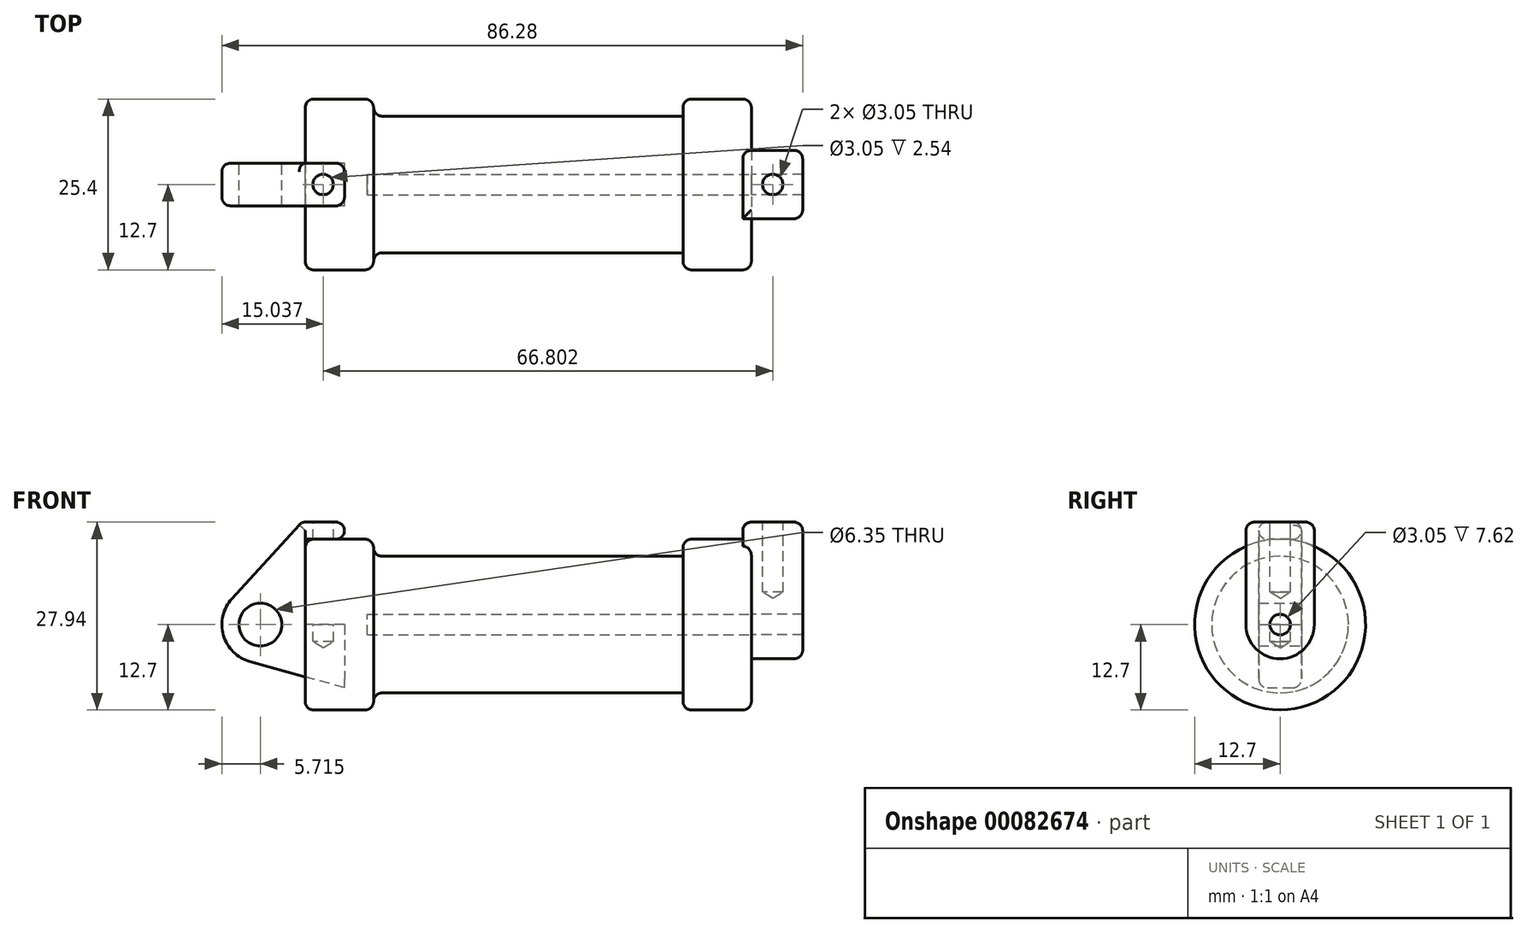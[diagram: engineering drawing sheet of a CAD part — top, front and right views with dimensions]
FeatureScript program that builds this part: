
annotation { "Feature Type Name" : "Feature", "Feature Type Description" : "" }
export const myFeature = defineFeature(function(context is Context, id is Id, definition is map)
    precondition{}
    {
        {
            var Q0;
            Q0=qCreatedBy(makeId("Front.planeOp"),FACE);
            var sketch = newSketch(context, id + "F0", { "sketchPlane" : qUnion([Q0])});
            skLineSegment(sketch, "E0", {"start": v(0, 0) * mm, "end": v(0, 12.7) * mm});
            skLineSegment(sketch, "E1", {"start": v(0, 12.7) * mm, "end": v(10.16, 12.7) * mm});
            skLineSegment(sketch, "E2", {"start": v(10.16, 12.7) * mm, "end": v(10.16, 10.16) * mm});
            skLineSegment(sketch, "E3", {"start": v(10.16, 10.16) * mm, "end": v(56.13, 10.16) * mm});
            skLineSegment(sketch, "E4", {"start": v(56.13, 10.16) * mm, "end": v(56.13, 12.7) * mm});
            skLineSegment(sketch, "E5", {"start": v(56.13, 12.7) * mm, "end": v(66.3, 12.7) * mm});
            skLineSegment(sketch, "E6", {"start": v(66.3, 12.7) * mm, "end": v(66.3, 0) * mm});
            skLineSegment(sketch, "E7", {"start": v(66.3, 0) * mm, "end": v(0, 0) * mm});
            skLineSegment(sketch, "E8", {"start": v(5.84, 15.24) * mm, "end": v(-0.5, 15.24) * mm});
            skLineSegment(sketch, "E9", {"start": v(-0.5, 15.24) * mm, "end": v(-10.88, 3.85) * mm});
            skLineSegment(sketch, "E10", {"start": v(0, 0) * mm, "end": v(-6.65, 0) * mm});
            skCircle(sketch, "E11", {"center": v(-6.65, 0) * mm, "radius": 5.72 * mm});
            skCircle(sketch, "E12", {"center": v(-6.65, 0) * mm, "radius": 3.18 * mm});
            skLineSegment(sketch, "E13", {"start": v(5.84, 15.24) * mm, "end": v(5.84, -9.4) * mm});
            skLineSegment(sketch, "E14", {"start": v(5.84, -9.4) * mm, "end": v(-8.18, -5.5) * mm});
            skSolve(sketch);
        }
        {
            var Q0;
            {var subQ0=sQuery(id+"F0.wireOp",EDGE,"E2");Q0=makeQuery(id+"F0.imprint","IMPRINT",FACE,{"disambiguationData":[TD([[makeQuery(id+"F0.imprint","IMPRINT",EDGE,{"derivedFrom":subQ0}),-1.0]])]});}
            var Q1;
            {var subQ0=sQuery(id+"F0.wireOp",EDGE,"E0");Q1=makeQuery(id+"F0.imprint","IMPRINT",FACE,{"disambiguationData":[TD([[makeQuery(id+"F0.imprint","IMPRINT",EDGE,{"derivedFrom":subQ0}),-1.0]])]});}
            var Q2;
            Q2=sQuery(id+"F0.wireOp",EDGE,"E7");
            revolve(context, id + "F1", {"entities" : qUnion([Q0, Q1]), "axis" : qUnion([Q2]), "revolveType" : RevolveType.FULL});
        }
        {
            var Q0;
            {var subQ3=sQuery(id+"F0.wireOp",EDGE,"E0");Q0=makeQuery(id+"F0.imprint","IMPRINT",FACE,{"disambiguationData":[TD([[makeQuery(id+"F0.imprint","IMPRINT",EDGE,{"derivedFrom":subQ3}),1.0]])]});}
            var Q1;
            {var subQ0=sQuery(id+"F0.wireOp",EDGE,"E14");Q1=makeQuery(id+"F0.imprint","IMPRINT",FACE,{"disambiguationData":[TD([[makeQuery(id+"F0.imprint","IMPRINT",EDGE,{"derivedFrom":subQ0}),-1.0]])]});}
            var Q2;
            {var subQ4=sQuery(id+"F0.wireOp",EDGE,"E12");Q2=makeQuery(id+"F0.imprint","IMPRINT",FACE,{"disambiguationData":[TD([[makeQuery(id+"F0.imprint","IMPRINT",EDGE,{"derivedFrom":subQ4}),-1.0]])]});}
            extrude(context, id + "F2", {"entities" : qUnion([Q0, Q1, Q2]), "endBound" : BoundingType.SYMMETRIC, "depth" : 6.35 * mm});
        }
        {
            var Q0;
            Q0=makeQuery(id+"F1.opRevolve","SWEPT_FACE",FACE,{"disambiguationData":[OSD([sQuery(id+"F0.wireOp",EDGE,"E6")])]});
            var sketch = newSketch(context, id + "F3", { "sketchPlane" : qUnion([Q0])});
            skCircle(sketch, "E15", {"center": v(0, 0) * mm, "radius": 5.08 * mm});
            skCircle(sketch, "E16", {"center": v(0, 0) * mm, "radius": 1.52 * mm});
            skLineSegment(sketch, "E17", {"start": v(-5.08, 0) * mm, "end": v(-5.08, 15.24) * mm});
            skLineSegment(sketch, "E18", {"start": v(5.08, 0) * mm, "end": v(5.08, 15.24) * mm});
            skLineSegment(sketch, "E19", {"start": v(-5.08, 15.24) * mm, "end": v(5.08, 15.24) * mm});
            skSolve(sketch);
        }
        {
            var Q0;
            Q0=makeQuery(id+"F3.imprint","IMPRINT",FACE,{"disambiguationData":[TD([[makeQuery(id+"F3.imprint","IMPRINT",EDGE,{"derivedFrom":sQuery(id+"F3.wireOp",EDGE,"E16")}),-1.0]])]});
            var Q1;
            {var subQ0=sQuery(id+"F3.wireOp",EDGE,"E17");var subQ1=sQuery(id+"F3.wireOp",EDGE,"E15");var subQ2=makeQuery(id+"F3.imprint","INTERSECT",VERTEX,{"derivedFrom":[subQ1,subQ0]});Q1=makeQuery(id+"F3.imprint","IMPRINT",FACE,{"disambiguationData":[TD([[makeQuery(id+"F3.imprint","IMPRINT",EDGE,{"disambiguationData":[TD([[subQ2,1.0]])],"derivedFrom":subQ1}),-1.0]])]});}
            var Q2;
            {var subQ0=sQuery(id+"F3.wireOp",EDGE,"E19");Q2=makeQuery(id+"F3.imprint","IMPRINT",FACE,{"disambiguationData":[TD([[makeQuery(id+"F3.imprint","IMPRINT",EDGE,{"derivedFrom":subQ0}),-1.0]])]});}
            extrude(context, id + "F4", {"entities" : qUnion([Q0, Q1, Q2]), "operationType" : NewBodyOperationType.ADD, "depth" : 7.62 * mm, "hasSecondDirection" : true, "secondDirectionOppositeDirection" : true, "secondDirectionDepth" : 1.27 * mm});
        }
        {
            var Q0;
            Q0=makeQuery(id+"F4.boolean.opBoolean","SPLIT",FACE,{"disambiguationData":[TD([makeQuery(id+"F4.opExtrude","SWEPT_FACE",FACE,{"disambiguationData":[OSD([sQuery(id+"F3.wireOp",EDGE,"E16")])]})])],"derivedFrom":makeQuery(id+"F1.opRevolve","SWEPT_FACE",FACE,{"disambiguationData":[OSD([sQuery(id+"F0.wireOp",EDGE,"E6")])]})});
            var sketch = newSketch(context, id + "F5", { "sketchPlane" : qUnion([Q0])});
            skCircle(sketch, "E20", {"center": v(0, 0) * mm, "radius": 1.52 * mm});
            skSolve(sketch);
        }
        {
            var Q0;
            Q0=makeQuery(id+"F5.imprint","IMPRINT",FACE,{"disambiguationData":[TD([[makeQuery(id+"F5.imprint","IMPRINT",EDGE,{"derivedFrom":sQuery(id+"F5.wireOp",EDGE,"E20")}),1.0]])]});
            extrude(context, id + "F6", {"entities" : qUnion([Q0]), "oppositeDirection" : true, "depth" : 57.04 * mm});
        }
        {
            var Q0;
            Q0=makeQuery(id+"F2.opExtrude","SWEPT_FACE",FACE,{"disambiguationData":[OSD([sQuery(id+"F0.wireOp",EDGE,"E8")])]});
            var sketch = newSketch(context, id + "F7", { "sketchPlane" : qUnion([Q0])});
            skLineSegment(sketch, "E21", {"start": v(-0.5, 3.18) * mm, "end": v(5.84, -3.18) * mm, "construction": true});
            skLineSegment(sketch, "E22", {"start": v(5.84, 3.18) * mm, "end": v(-0.5, -3.18) * mm, "construction": true});
            skCircle(sketch, "E23", {"center": v(2.67, 0) * mm, "radius": 1.53 * mm});
            skSolve(sketch);
        }
        {
            var Q0;
            Q0=sQuery(id+"F7.wireOp",VERTEX,"E23.center");
            var Q1;
            Q1=makeQuery(id+"F2.opExtrude","SWEPT_BODY",BODY,{"disambiguationData":[OSD([sQuery(id+"F0.wireOp",EDGE,"E0"),sQuery(id+"F0.wireOp",EDGE,"E1"),sQuery(id+"F0.wireOp",EDGE,"E7"),sQuery(id+"F0.wireOp",EDGE,"E8"),sQuery(id+"F0.wireOp",EDGE,"E9"),sQuery(id+"F0.wireOp",EDGE,"E11"),sQuery(id+"F0.wireOp",EDGE,"E12"),sQuery(id+"F0.wireOp",EDGE,"E13"),sQuery(id+"F0.wireOp",EDGE,"E14")])]});
            hole(context, id + "F8", {"style" : HoleStyle.SIMPLE, "endStyle" : HoleEndStyle.BLIND, "holeDiameter" : 3.05 * mm, "holeDepth" : 17.78 * mm, "locations" : qUnion([Q0]), "scope" : qUnion([Q1])});
        }
        {
            var Q0;
            Q0=makeQuery(id+"F4.opExtrude","SWEPT_FACE",FACE,{"disambiguationData":[OSD([sQuery(id+"F3.wireOp",EDGE,"E19")])]});
            var sketch = newSketch(context, id + "F9", { "sketchPlane" : qUnion([Q0])});
            skLineSegment(sketch, "E24", {"start": v(65.02, 5.08) * mm, "end": v(73.91, -5.08) * mm, "construction": true});
            skLineSegment(sketch, "E25", {"start": v(73.91, -5.08) * mm, "end": v(65.02, -5.08) * mm, "construction": true});
            skLineSegment(sketch, "E26", {"start": v(65.02, -5.08) * mm, "end": v(73.91, 5.08) * mm, "construction": true});
            skCircle(sketch, "E27", {"center": v(69.47, 0) * mm, "radius": 1.53 * mm});
            skSolve(sketch);
        }
        {
            var Q0;
            Q0=sQuery(id+"F9.wireOp",VERTEX,"E27.center");
            var Q1;
            Q1=makeQuery(id+"F1.opRevolve","SWEPT_BODY",BODY,{"disambiguationData":[OSD([sQuery(id+"F0.wireOp",EDGE,"E0"),sQuery(id+"F0.wireOp",EDGE,"E1"),sQuery(id+"F0.wireOp",EDGE,"E2"),sQuery(id+"F0.wireOp",EDGE,"E3"),sQuery(id+"F0.wireOp",EDGE,"E4"),sQuery(id+"F0.wireOp",EDGE,"E5"),sQuery(id+"F0.wireOp",EDGE,"E6"),sQuery(id+"F0.wireOp",EDGE,"E7")])]});
            hole(context, id + "F10", {"style" : HoleStyle.SIMPLE, "endStyle" : HoleEndStyle.BLIND, "holeDiameter" : 3.05 * mm, "holeDepth" : 10.4 * mm, "locations" : qUnion([Q0]), "scope" : qUnion([Q1])});
        }
        {
            var Q0;
            Q0=makeQuery(id+"F1.opRevolve","SWEPT_EDGE",EDGE,{"disambiguationData":[OSD([sQuery(id+"F0.wireOp",EDGE,"E1"),sQuery(id+"F0.wireOp",EDGE,"E2")])]});
            var Q1;
            Q1=makeQuery(id+"F1.opRevolve","SWEPT_EDGE",EDGE,{"disambiguationData":[OSD([sQuery(id+"F0.wireOp",EDGE,"E2"),sQuery(id+"F0.wireOp",EDGE,"E3")])]});
            var Q2;
            Q2=makeQuery(id+"F1.opRevolve","SWEPT_EDGE",EDGE,{"disambiguationData":[OSD([sQuery(id+"F0.wireOp",EDGE,"E4"),sQuery(id+"F0.wireOp",EDGE,"E5")])]});
            var Q3;
            Q3=makeQuery(id+"F1.opRevolve","SWEPT_EDGE",EDGE,{"disambiguationData":[OSD([sQuery(id+"F0.wireOp",EDGE,"E5"),sQuery(id+"F0.wireOp",EDGE,"E6")])]});
            var Q4;
            Q4=makeQuery(id+"F1.opRevolve","SWEPT_EDGE",EDGE,{"disambiguationData":[OSD([sQuery(id+"F0.wireOp",EDGE,"E0"),sQuery(id+"F0.wireOp",EDGE,"E1")])]});
            fillet(context, id + "F11", {"entities" : qUnion([Q0, Q1, Q2, Q3, Q4]), "radius" : 1.27 * mm, "tangentPropagation" : true, "allowEdgeOverflow" : false});
        }
        {
            var Q0;
            Q0=makeQuery(id+"F4.opExtrude","SWEPT_EDGE",EDGE,{"disambiguationData":[OSD([sQuery(id+"F3.wireOp",EDGE,"E17"),sQuery(id+"F3.wireOp",EDGE,"E19")])]});
            var Q1;
            Q1=makeQuery(id+"F4.opExtrude","CAP_EDGE",EDGE,{"disambiguationData":[OSD([sQuery(id+"F3.wireOp",EDGE,"E19")])],"isStart":false});
            var Q2;
            Q2=makeQuery(id+"F4.opExtrude","CAP_EDGE",EDGE,{"disambiguationData":[OSD([sQuery(id+"F3.wireOp",EDGE,"E17")])],"isStart":false});
            var Q3;
            Q3=makeQuery(id+"F4.opExtrude","CAP_EDGE",EDGE,{"disambiguationData":[OSD([sQuery(id+"F3.wireOp",EDGE,"E15")])],"isStart":false});
            var Q4;
            Q4=makeQuery(id+"F4.opExtrude","CAP_EDGE",EDGE,{"disambiguationData":[OSD([sQuery(id+"F3.wireOp",EDGE,"E18")])],"isStart":false});
            var Q5;
            Q5=makeQuery(id+"F4.opExtrude","CAP_EDGE",EDGE,{"disambiguationData":[OSD([sQuery(id+"F3.wireOp",EDGE,"E18")])],"isStart":true});
            var Q6;
            Q6=makeQuery(id+"F4.opExtrude","CAP_EDGE",EDGE,{"disambiguationData":[OSD([sQuery(id+"F3.wireOp",EDGE,"E19")])],"isStart":true});
            var Q7;
            Q7=makeQuery(id+"F4.opExtrude","SWEPT_EDGE",EDGE,{"disambiguationData":[OSD([sQuery(id+"F3.wireOp",EDGE,"E18"),sQuery(id+"F3.wireOp",EDGE,"E19")])]});
            fillet(context, id + "F12", {"entities" : qUnion([Q0, Q1, Q2, Q3, Q4, Q5, Q6, Q7]), "radius" : 1.27 * mm, "tangentPropagation" : true, "allowEdgeOverflow" : false});
        }
        {
            var Q0;
            Q0=makeQuery(id+"F2.opExtrude","SWEPT_EDGE",EDGE,{"disambiguationData":[OSD([sQuery(id+"F0.wireOp",EDGE,"E8"),sQuery(id+"F0.wireOp",EDGE,"E9")])]});
            var Q1;
            Q1=makeQuery(id+"F2.opExtrude","CAP_EDGE",EDGE,{"disambiguationData":[OSD([sQuery(id+"F0.wireOp",EDGE,"E8")])],"isStart":false});
            var Q2;
            Q2=makeQuery(id+"F2.opExtrude","CAP_EDGE",EDGE,{"disambiguationData":[OSD([sQuery(id+"F0.wireOp",EDGE,"E9")])],"isStart":false});
            var Q3;
            Q3=makeQuery(id+"F2.opExtrude","CAP_EDGE",EDGE,{"disambiguationData":[OSD([sQuery(id+"F0.wireOp",EDGE,"E11")])],"isStart":false});
            var Q4;
            Q4=makeQuery(id+"F2.opExtrude","CAP_EDGE",EDGE,{"disambiguationData":[OSD([sQuery(id+"F0.wireOp",EDGE,"E14")])],"isStart":false});
            var Q5;
            Q5=makeQuery(id+"F2.opExtrude","CAP_EDGE",EDGE,{"disambiguationData":[OSD([sQuery(id+"F0.wireOp",EDGE,"E11")])],"isStart":true});
            var Q6;
            Q6=makeQuery(id+"F2.opExtrude","CAP_EDGE",EDGE,{"disambiguationData":[OSD([sQuery(id+"F0.wireOp",EDGE,"E9")])],"isStart":true});
            var Q7;
            Q7=makeQuery(id+"F2.opExtrude","CAP_EDGE",EDGE,{"disambiguationData":[OSD([sQuery(id+"F0.wireOp",EDGE,"E14")])],"isStart":true});
            var Q8;
            {var subQ0=sQuery(id+"F0.wireOp",EDGE,"E13");Q8=makeQuery(id+"F2.opExtrude","CAP_EDGE",EDGE,{"disambiguationData":[OSD([subQ0]),TDD([makeQuery(id+"F0.imprint","IMPRINT",EDGE,{"disambiguationData":[TD([[makeQuery(id+"F0.imprint","INTERSECT",VERTEX,{"derivedFrom":[sQuery(id+"F0.wireOp",EDGE,"E8"),subQ0]}),-1.0]])],"derivedFrom":subQ0})])],"isStart":true});}
            var Q9;
            Q9=makeQuery(id+"F2.opExtrude","SWEPT_EDGE",EDGE,{"disambiguationData":[OSD([sQuery(id+"F0.wireOp",EDGE,"E8"),sQuery(id+"F0.wireOp",EDGE,"E13")])]});
            fillet(context, id + "F13", {"entities" : qUnion([Q0, Q1, Q2, Q3, Q4, Q5, Q6, Q7, Q8, Q9]), "radius" : 1.27 * mm, "tangentPropagation" : true, "allowEdgeOverflow" : false});
        }
        {
            var Q0;
            Q0=makeQuery(id+"F2.opExtrude","CAP_EDGE",EDGE,{"disambiguationData":[OSD([sQuery(id+"F0.wireOp",EDGE,"E8")])],"isStart":true});
            var Q1;
            {var subQ0=sQuery(id+"F0.wireOp",EDGE,"E8");Q1=makeQuery(id+"F13.opFillet","BLEND_EDGE",EDGE,{"blendedFrom":[makeQuery(id+"F2.opExtrude","SWEPT_EDGE",EDGE,{"disambiguationData":[OSD([subQ0,sQuery(id+"F0.wireOp",EDGE,"E13")])]}),makeQuery(id+"F2.opExtrude","CAP_EDGE",EDGE,{"disambiguationData":[OSD([subQ0])],"isStart":false})],"blendedInto":[]});}
            fillet(context, id + "F14", {"entities" : qUnion([Q0, Q1]), "radius" : 1.27 * mm, "tangentPropagation" : true, "allowEdgeOverflow" : false});
        }
        {
            var Q0;
            Q0=makeQuery(id+"F2.opExtrude","CAP_EDGE",EDGE,{"disambiguationData":[OSD([sQuery(id+"F0.wireOp",EDGE,"E1")])],"isStart":true});
            fillet(context, id + "F15", {"entities" : qUnion([Q0]), "radius" : 1.27 * mm, "tangentPropagation" : true, "allowEdgeOverflow" : false});
        }
    });
